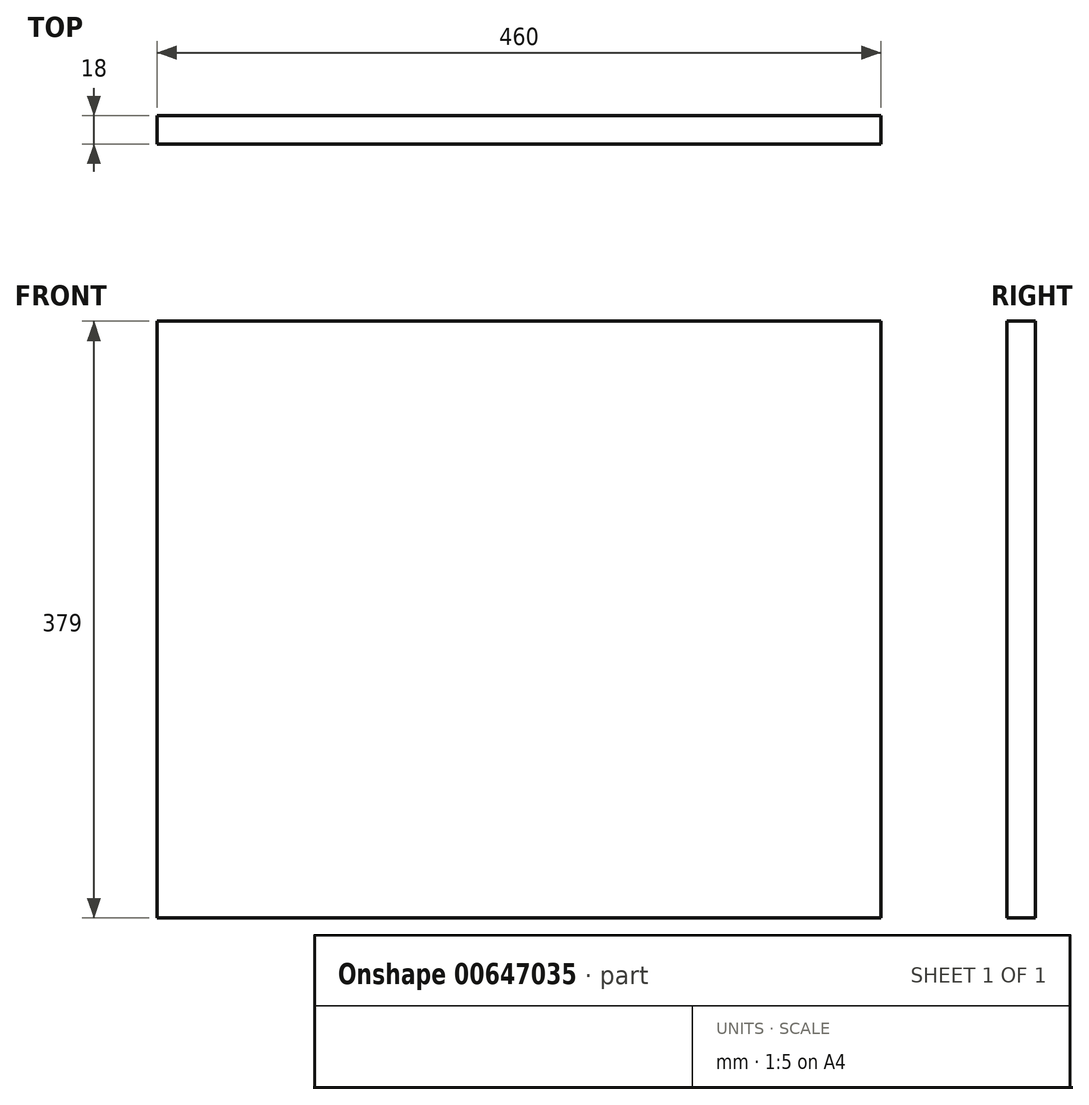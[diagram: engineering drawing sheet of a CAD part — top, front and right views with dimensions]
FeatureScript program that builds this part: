
annotation { "Feature Type Name" : "Feature", "Feature Type Description" : "" }
export const myFeature = defineFeature(function(context is Context, id is Id, definition is map)
    precondition{}
    {
        {
            var Q0;
            Q0=qCreatedBy(makeId("Front.planeOp"),FACE);
            var sketch = newSketch(context, id + "F0", { "sketchPlane" : qUnion([Q0])});
            skLineSegment(sketch, "E0.bottom", {"start": v(-230, 379) * mm, "end": v(230, 379) * mm});
            skLineSegment(sketch, "E0.top", {"start": v(-230, 0) * mm, "end": v(230, 0) * mm});
            skLineSegment(sketch, "E0.left", {"start": v(-230, 379) * mm, "end": v(-230, 0) * mm});
            skLineSegment(sketch, "E0.right", {"start": v(230, 379) * mm, "end": v(230, 0) * mm});
            skSolve(sketch);
        }
        {
            var Q0;
            Q0=makeQuery(id+"F0.imprint","IMPRINT",FACE,{"disambiguationData":[TD([[makeQuery(id+"F0.imprint","IMPRINT",EDGE,{"derivedFrom":sQuery(id+"F0.wireOp",EDGE,"E0.bottom")}),-1.0]])]});
            extrude(context, id + "F1", {"entities" : qUnion([Q0]), "depth" : 18 * mm, "offsetDistance" : 25 * mm});
        }
    });
